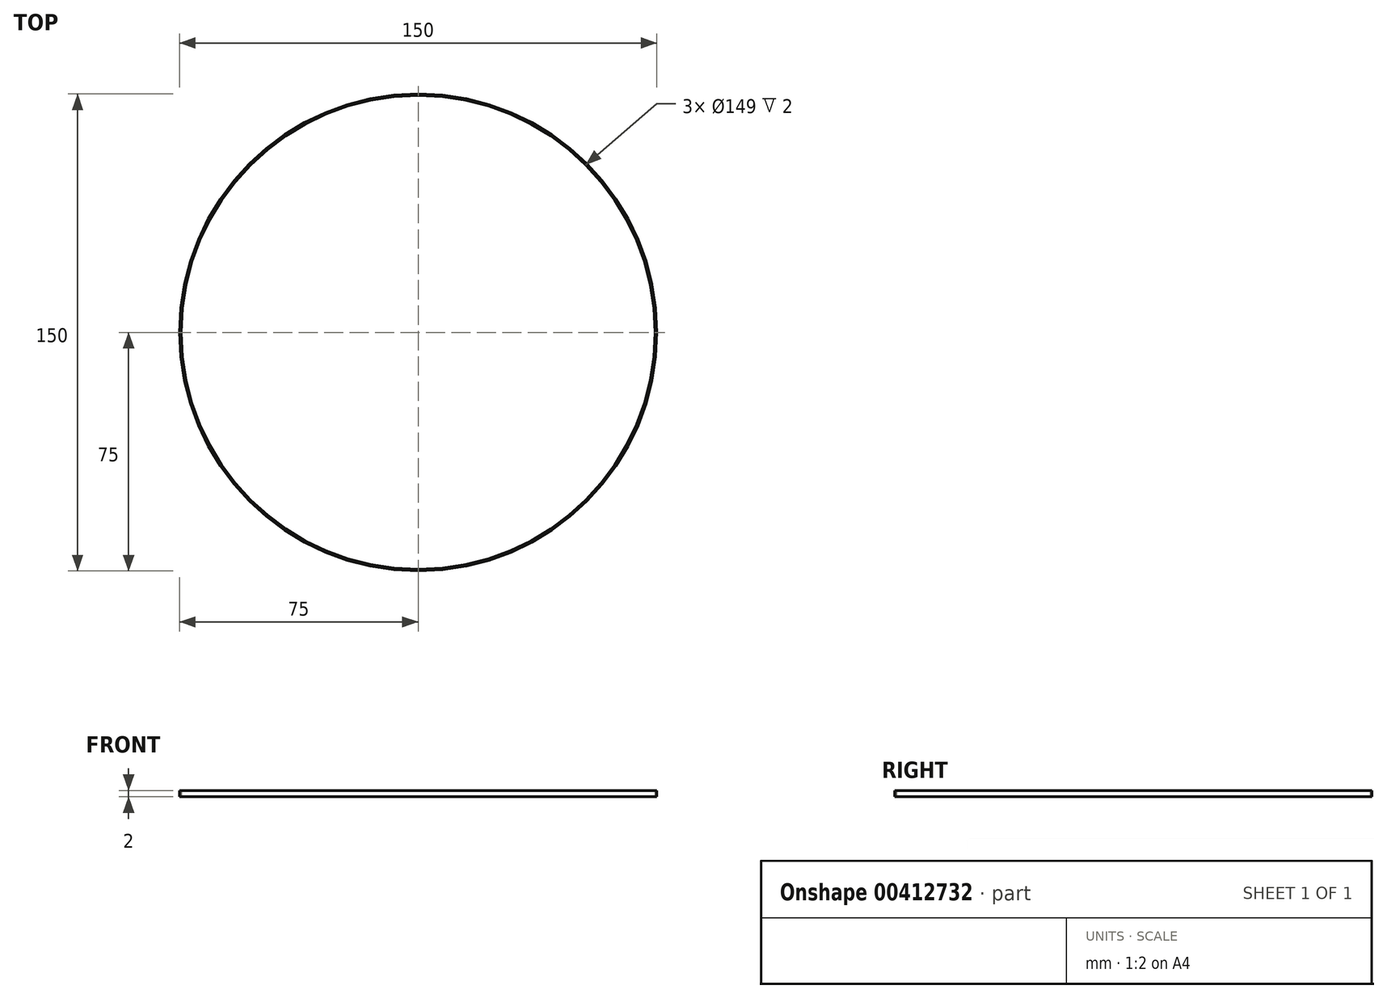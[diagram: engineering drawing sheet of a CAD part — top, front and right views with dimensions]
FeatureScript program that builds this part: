
annotation { "Feature Type Name" : "Feature", "Feature Type Description" : "" }
export const myFeature = defineFeature(function(context is Context, id is Id, definition is map)
    precondition{}
    {
        {
            var Q0;
            Q0=qCreatedBy(makeId("Top.planeOp"),FACE);
            var sketch = newSketch(context, id + "F0", { "sketchPlane" : qUnion([Q0])});
            skCircle(sketch, "E0", {"center": v(0, 0) * mm, "radius": 74.5 * mm});
            skCircle(sketch, "E1", {"center": v(0, 0) * mm, "radius": 75 * mm});
            skSolve(sketch);
        }
        {
            var Q0;
            Q0=makeQuery(id+"F0.imprint","IMPRINT",FACE,{"disambiguationData":[TD([[makeQuery(id+"F0.imprint","IMPRINT",EDGE,{"derivedFrom":sQuery(id+"F0.wireOp",EDGE,"E0")}),-1.0]])]});
            extrude(context, id + "F1", {"entities" : qUnion([Q0]), "depth" : 2 * mm, "offsetDistance" : 25 * mm});
        }
    });
